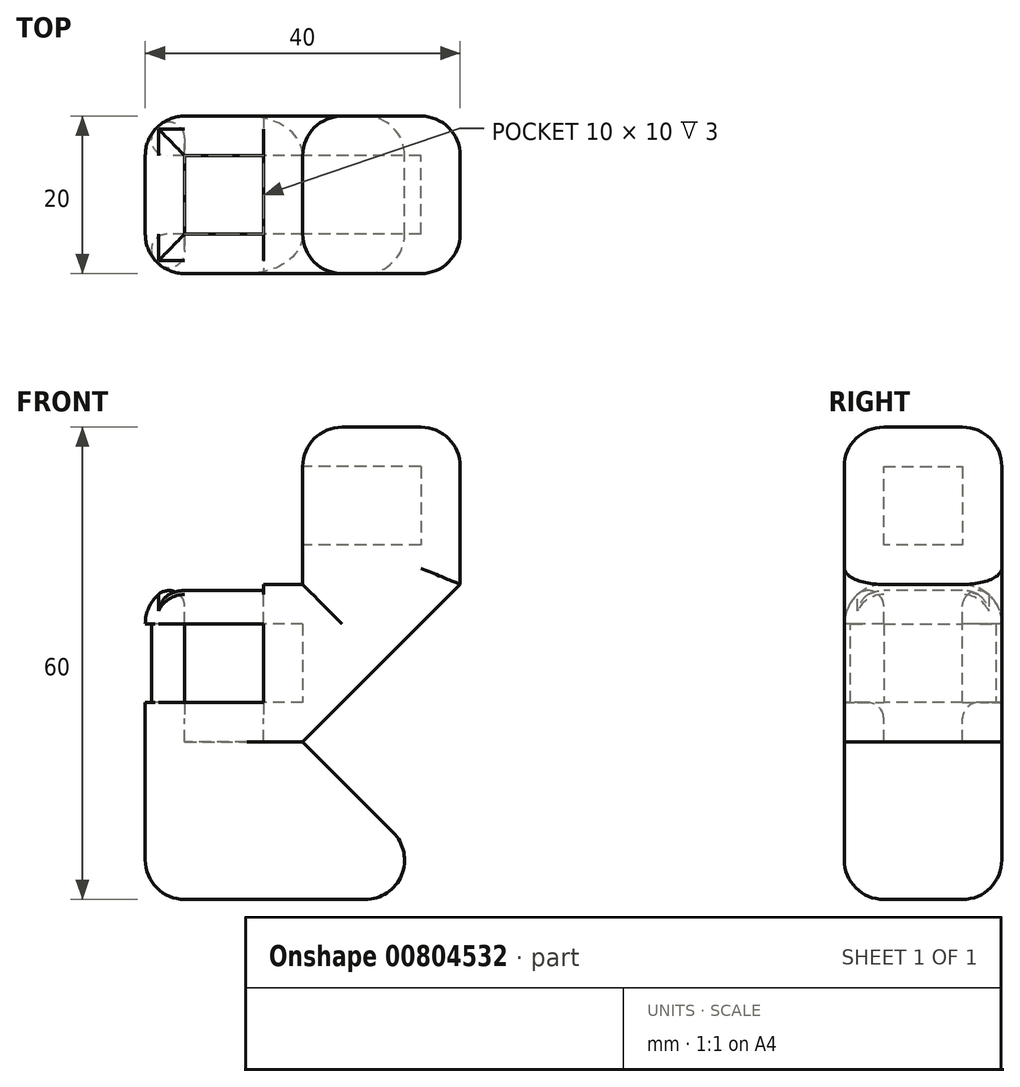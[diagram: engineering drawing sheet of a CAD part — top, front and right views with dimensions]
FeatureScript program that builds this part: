
annotation { "Feature Type Name" : "Feature", "Feature Type Description" : "" }
export const myFeature = defineFeature(function(context is Context, id is Id, definition is map)
    precondition{}
    {
        {
            var Q0;
            Q0=qCreatedBy(makeId("Front.planeOp"),FACE);
            var sketch = newSketch(context, id + "F0", { "sketchPlane" : qUnion([Q0])});
            skLineSegment(sketch, "E0.bottom", {"start": v(-64.5, 36.94) * mm, "end": v(-44.5, 36.94) * mm});
            skLineSegment(sketch, "E0.top", {"start": v(-64.5, 16.94) * mm, "end": v(-44.5, 16.94) * mm});
            skLineSegment(sketch, "E0.left", {"start": v(-64.5, 36.94) * mm, "end": v(-64.5, 16.94) * mm});
            skLineSegment(sketch, "E0.right", {"start": v(-44.5, 36.94) * mm, "end": v(-44.5, 16.94) * mm});
            skLineSegment(sketch, "E1.top", {"start": v(-64.5, 56.94) * mm, "end": v(-44.5, 56.94) * mm});
            skLineSegment(sketch, "E1.left", {"start": v(-64.5, 36.94) * mm, "end": v(-64.5, 56.94) * mm});
            skLineSegment(sketch, "E1.right", {"start": v(-44.5, 36.94) * mm, "end": v(-44.5, 56.94) * mm});
            skLineSegment(sketch, "E2", {"start": v(-44.5, 56.94) * mm, "end": v(-24.5, 56.94) * mm});
            skLineSegment(sketch, "E3", {"start": v(-24.5, 56.94) * mm, "end": v(-44.5, 36.94) * mm});
            skLineSegment(sketch, "E4.left", {"start": v(-44.5, 56.94) * mm, "end": v(-44.5, 56.94) * mm});
            skLineSegment(sketch, "E4.right", {"start": v(-24.5, 56.94) * mm, "end": v(-24.5, 56.94) * mm});
            skLineSegment(sketch, "E5.top", {"start": v(-44.5, 76.94) * mm, "end": v(-24.5, 76.94) * mm});
            skLineSegment(sketch, "E5.left", {"start": v(-44.5, 56.94) * mm, "end": v(-44.5, 76.94) * mm});
            skLineSegment(sketch, "E5.right", {"start": v(-24.5, 56.94) * mm, "end": v(-24.5, 76.94) * mm});
            skLineSegment(sketch, "E6", {"start": v(-44.5, 16.94) * mm, "end": v(-24.5, 16.94) * mm});
            skLineSegment(sketch, "E7", {"start": v(-24.5, 16.94) * mm, "end": v(-44.5, 36.94) * mm});
            skSolve(sketch);
        }
        {
            var Q0;
            Q0=makeQuery(id+"F0.imprint","IMPRINT",FACE,{"disambiguationData":[TD([[makeQuery(id+"F0.imprint","IMPRINT",EDGE,{"derivedFrom":sQuery(id+"F0.wireOp",EDGE,"E0.right")}),1.0]])]});
            var Q1;
            Q1=makeQuery(id+"F0.imprint","IMPRINT",FACE,{"disambiguationData":[TD([[makeQuery(id+"F0.imprint","IMPRINT",EDGE,{"derivedFrom":sQuery(id+"F0.wireOp",EDGE,"E0.top")}),1.0]])]});
            var Q2;
            Q2=makeQuery(id+"F0.imprint","IMPRINT",FACE,{"disambiguationData":[TD([[makeQuery(id+"F0.imprint","IMPRINT",EDGE,{"derivedFrom":sQuery(id+"F0.wireOp",EDGE,"E0.bottom")}),1.0]])]});
            var Q3;
            Q3=makeQuery(id+"F0.imprint","IMPRINT",FACE,{"disambiguationData":[TD([[makeQuery(id+"F0.imprint","IMPRINT",EDGE,{"derivedFrom":sQuery(id+"F0.wireOp",EDGE,"E1.right")}),-1.0]])]});
            var Q4;
            Q4=makeQuery(id+"F0.imprint","IMPRINT",FACE,{"disambiguationData":[TD([[makeQuery(id+"F0.imprint","IMPRINT",EDGE,{"derivedFrom":sQuery(id+"F0.wireOp",EDGE,"E2")}),1.0]])]});
            extrude(context, id + "F1", {"entities" : qUnion([Q0, Q1, Q2, Q3, Q4]), "depth" : 20 * mm, "offsetDistance" : 25 * mm});
        }
        {
            var Q0;
            Q0=makeQuery(id+"F1.opExtrude","SWEPT_FACE",FACE,{"disambiguationData":[OSD([sQuery(id+"F0.wireOp",EDGE,"E0.left"),sQuery(id+"F0.wireOp",EDGE,"E1.left")])]});
            var sketch = newSketch(context, id + "F2", { "sketchPlane" : qUnion([Q0])});
            skLineSegment(sketch, "E8", {"start": v(0, 56.94) * mm, "end": v(0, 36.94) * mm});
            skLineSegment(sketch, "E9", {"start": v(0, 36.94) * mm, "end": v(20, 36.94) * mm});
            skLineSegment(sketch, "E10", {"start": v(20, 36.94) * mm, "end": v(20, 56.94) * mm});
            skLineSegment(sketch, "E11", {"start": v(20, 56.94) * mm, "end": v(0, 56.94) * mm});
            skLineSegment(sketch, "E12.0", {"start": v(5, 51.94) * mm, "end": v(5, 41.94) * mm});
            skLineSegment(sketch, "E12.1", {"start": v(15, 51.94) * mm, "end": v(5, 51.94) * mm});
            skLineSegment(sketch, "E12.2", {"start": v(15, 41.94) * mm, "end": v(15, 51.94) * mm});
            skLineSegment(sketch, "E12.3", {"start": v(5, 41.94) * mm, "end": v(15, 41.94) * mm});
            skSolve(sketch);
        }
        {
            var Q0;
            Q0=makeQuery(id+"F2.imprint","IMPRINT",FACE,{"disambiguationData":[TD([[makeQuery(id+"F2.imprint","IMPRINT",EDGE,{"derivedFrom":sQuery(id+"F2.wireOp",EDGE,"E12.0")}),1.0]])]});
            extrude(context, id + "F3", {"entities" : qUnion([Q0]), "operationType" : NewBodyOperationType.REMOVE, "oppositeDirection" : true, "depth" : 20 * mm, "offsetDistance" : 25 * mm});
        }
        {
            var Q0;
            Q0=makeQuery(id+"F1.opExtrude","CAP_FACE",FACE,{"disambiguationData":[OSD([sQuery(id+"F0.wireOp",EDGE,"E0.top"),sQuery(id+"F0.wireOp",EDGE,"E0.left"),sQuery(id+"F0.wireOp",EDGE,"E1.top"),sQuery(id+"F0.wireOp",EDGE,"E1.left"),sQuery(id+"F0.wireOp",EDGE,"E3"),sQuery(id+"F0.wireOp",EDGE,"E5.top"),sQuery(id+"F0.wireOp",EDGE,"E5.left"),sQuery(id+"F0.wireOp",EDGE,"E5.right"),sQuery(id+"F0.wireOp",EDGE,"E6"),sQuery(id+"F0.wireOp",EDGE,"E7")])],"isStart":false});
            var sketch = newSketch(context, id + "F4", { "sketchPlane" : qUnion([Q0])});
            skLineSegment(sketch, "E13", {"start": v(-44.5, 36.94) * mm, "end": v(-64.5, 36.94) * mm});
            skLineSegment(sketch, "E14", {"start": v(-44.5, 36.94) * mm, "end": v(-44.5, 56.94) * mm});
            skLineSegment(sketch, "E15", {"start": v(-44.5, 56.94) * mm, "end": v(-64.5, 56.94) * mm});
            skLineSegment(sketch, "E16", {"start": v(-64.5, 56.94) * mm, "end": v(-64.5, 36.94) * mm});
            skLineSegment(sketch, "E17.0", {"start": v(-59.5, 51.94) * mm, "end": v(-59.5, 41.94) * mm});
            skLineSegment(sketch, "E17.1", {"start": v(-49.5, 51.94) * mm, "end": v(-59.5, 51.94) * mm});
            skLineSegment(sketch, "E17.2", {"start": v(-49.5, 41.94) * mm, "end": v(-49.5, 51.94) * mm});
            skLineSegment(sketch, "E17.3", {"start": v(-49.5, 41.94) * mm, "end": v(-59.5, 41.94) * mm});
            skSolve(sketch);
        }
        {
            var Q0;
            Q0=makeQuery(id+"F4.imprint","IMPRINT",FACE,{"disambiguationData":[TD([[makeQuery(id+"F4.imprint","IMPRINT",EDGE,{"derivedFrom":sQuery(id+"F4.wireOp",EDGE,"E17.0")}),1.0]])]});
            extrude(context, id + "F5", {"entities" : qUnion([Q0]), "operationType" : NewBodyOperationType.REMOVE, "oppositeDirection" : true, "depth" : 20 * mm, "offsetDistance" : 25 * mm});
        }
        {
            var Q0;
            Q0=makeQuery(id+"F1.opExtrude","SWEPT_FACE",FACE,{"disambiguationData":[OSD([sQuery(id+"F0.wireOp",EDGE,"E1.top")])]});
            var sketch = newSketch(context, id + "F6", { "sketchPlane" : qUnion([Q0])});
            skLineSegment(sketch, "E18.0", {"start": v(-49.5, -5) * mm, "end": v(-59.5, -5) * mm});
            skLineSegment(sketch, "E18.1", {"start": v(-49.5, -15) * mm, "end": v(-49.5, -5) * mm});
            skLineSegment(sketch, "E18.2", {"start": v(-59.5, -15) * mm, "end": v(-49.5, -15) * mm});
            skLineSegment(sketch, "E18.3", {"start": v(-59.5, -5) * mm, "end": v(-59.5, -15) * mm});
            skSolve(sketch);
        }
        {
            var Q0;
            Q0=makeQuery(id+"F6.imprint","IMPRINT",FACE,{"disambiguationData":[TD([[makeQuery(id+"F6.imprint","IMPRINT",EDGE,{"derivedFrom":sQuery(id+"F6.wireOp",EDGE,"E18.0")}),1.0]])]});
            extrude(context, id + "F7", {"entities" : qUnion([Q0]), "operationType" : NewBodyOperationType.REMOVE, "oppositeDirection" : true, "depth" : 20 * mm, "offsetDistance" : 25 * mm});
        }
        {
            var Q0;
            Q0=makeQuery(id+"F1.opExtrude","SWEPT_FACE",FACE,{"disambiguationData":[OSD([sQuery(id+"F0.wireOp",EDGE,"E5.left")])]});
            var sketch = newSketch(context, id + "F8", { "sketchPlane" : qUnion([Q0])});
            skLineSegment(sketch, "E19.0", {"start": v(5, 71.94) * mm, "end": v(5, 61.94) * mm});
            skLineSegment(sketch, "E19.1", {"start": v(15, 71.94) * mm, "end": v(5, 71.94) * mm});
            skLineSegment(sketch, "E19.2", {"start": v(15, 61.94) * mm, "end": v(15, 71.94) * mm});
            skLineSegment(sketch, "E19.3", {"start": v(5, 61.94) * mm, "end": v(15, 61.94) * mm});
            skSolve(sketch);
        }
        {
            var Q0;
            Q0=makeQuery(id+"F8.imprint","IMPRINT",FACE,{"disambiguationData":[TD([[makeQuery(id+"F8.imprint","IMPRINT",EDGE,{"derivedFrom":sQuery(id+"F8.wireOp",EDGE,"E19.0")}),1.0]])]});
            extrude(context, id + "F9", {"entities" : qUnion([Q0]), "operationType" : NewBodyOperationType.REMOVE, "oppositeDirection" : true, "depth" : 15 * mm, "offsetDistance" : 25 * mm});
        }
        {
            var Q0;
            Q0=makeQuery(id+"F1.opExtrude","CAP_EDGE",EDGE,{"disambiguationData":[OSD([sQuery(id+"F0.wireOp",EDGE,"E0.left"),sQuery(id+"F0.wireOp",EDGE,"E1.left")])],"isStart":false});
            var Q1;
            Q1=makeQuery(id+"F1.opExtrude","CAP_EDGE",EDGE,{"disambiguationData":[OSD([sQuery(id+"F0.wireOp",EDGE,"E0.left"),sQuery(id+"F0.wireOp",EDGE,"E1.left")])],"isStart":true});
            var Q2;
            Q2=makeQuery(id+"F1.opExtrude","SWEPT_EDGE",EDGE,{"disambiguationData":[OSD([sQuery(id+"F0.wireOp",EDGE,"E1.top"),sQuery(id+"F0.wireOp",EDGE,"E1.left")])]});
            var Q3;
            Q3=makeQuery(id+"F1.opExtrude","CAP_EDGE",EDGE,{"disambiguationData":[OSD([sQuery(id+"F0.wireOp",EDGE,"E1.top")])],"isStart":false});
            var Q4;
            Q4=makeQuery(id+"F1.opExtrude","CAP_EDGE",EDGE,{"disambiguationData":[OSD([sQuery(id+"F0.wireOp",EDGE,"E1.top")])],"isStart":true});
            var Q5;
            Q5=makeQuery(id+"F1.opExtrude","CAP_EDGE",EDGE,{"disambiguationData":[OSD([sQuery(id+"F0.wireOp",EDGE,"E7")])],"isStart":false});
            var Q6;
            Q6=makeQuery(id+"F1.opExtrude","CAP_EDGE",EDGE,{"disambiguationData":[OSD([sQuery(id+"F0.wireOp",EDGE,"E3")])],"isStart":false});
            var Q7;
            Q7=makeQuery(id+"F1.opExtrude","CAP_EDGE",EDGE,{"disambiguationData":[OSD([sQuery(id+"F0.wireOp",EDGE,"E7")])],"isStart":true});
            var Q8;
            Q8=makeQuery(id+"F1.opExtrude","CAP_EDGE",EDGE,{"disambiguationData":[OSD([sQuery(id+"F0.wireOp",EDGE,"E3")])],"isStart":true});
            var Q9;
            Q9=makeQuery(id+"F1.opExtrude","CAP_EDGE",EDGE,{"disambiguationData":[OSD([sQuery(id+"F0.wireOp",EDGE,"E5.right")])],"isStart":false});
            var Q10;
            Q10=makeQuery(id+"F1.opExtrude","CAP_EDGE",EDGE,{"disambiguationData":[OSD([sQuery(id+"F0.wireOp",EDGE,"E5.right")])],"isStart":true});
            var Q11;
            Q11=makeQuery(id+"F1.opExtrude","SWEPT_EDGE",EDGE,{"disambiguationData":[OSD([sQuery(id+"F0.wireOp",EDGE,"E5.top"),sQuery(id+"F0.wireOp",EDGE,"E5.left")])]});
            var Q12;
            Q12=makeQuery(id+"F1.opExtrude","CAP_EDGE",EDGE,{"disambiguationData":[OSD([sQuery(id+"F0.wireOp",EDGE,"E5.top")])],"isStart":false});
            var Q13;
            Q13=makeQuery(id+"F1.opExtrude","SWEPT_EDGE",EDGE,{"disambiguationData":[OSD([sQuery(id+"F0.wireOp",EDGE,"E5.top"),sQuery(id+"F0.wireOp",EDGE,"E5.right")])]});
            var Q14;
            Q14=makeQuery(id+"F1.opExtrude","CAP_EDGE",EDGE,{"disambiguationData":[OSD([sQuery(id+"F0.wireOp",EDGE,"E5.top")])],"isStart":true});
            var Q15;
            Q15=makeQuery(id+"F1.opExtrude","CAP_EDGE",EDGE,{"disambiguationData":[OSD([sQuery(id+"F0.wireOp",EDGE,"E0.top"),sQuery(id+"F0.wireOp",EDGE,"E6")])],"isStart":false});
            var Q16;
            Q16=makeQuery(id+"F1.opExtrude","CAP_EDGE",EDGE,{"disambiguationData":[OSD([sQuery(id+"F0.wireOp",EDGE,"E0.top"),sQuery(id+"F0.wireOp",EDGE,"E6")])],"isStart":true});
            var Q17;
            Q17=makeQuery(id+"F1.opExtrude","SWEPT_EDGE",EDGE,{"disambiguationData":[OSD([sQuery(id+"F0.wireOp",EDGE,"E6"),sQuery(id+"F0.wireOp",EDGE,"E7")])]});
            var Q18;
            Q18=makeQuery(id+"F1.opExtrude","SWEPT_EDGE",EDGE,{"disambiguationData":[OSD([sQuery(id+"F0.wireOp",EDGE,"E0.top"),sQuery(id+"F0.wireOp",EDGE,"E0.left")])]});
            fillet(context, id + "F10", {"entities" : qUnion([Q0, Q1, Q2, Q3, Q4, Q5, Q6, Q7, Q8, Q9, Q10, Q11, Q12, Q13, Q14, Q15, Q16, Q17, Q18]), "radius" : 5 * mm, "tangentPropagation" : true, "allowEdgeOverflow" : false});
        }
        {
            var Q0;
            Q0=makeQuery(id+"F5.boolean.opBoolean","COPY",EDGE,{"derivedFrom":makeQuery(id+"F5.opExtrude","CAP_EDGE",EDGE,{"disambiguationData":[OSD([sQuery(id+"F4.wireOp",EDGE,"E17.3")])],"isStart":true})});
            var Q1;
            Q1=makeQuery(id+"F3.boolean.opBoolean","COPY",EDGE,{"derivedFrom":makeQuery(id+"F3.opExtrude","CAP_EDGE",EDGE,{"disambiguationData":[OSD([sQuery(id+"F2.wireOp",EDGE,"E12.3")])],"isStart":true})});
            var Q2;
            Q2=makeQuery(id+"F5.boolean.opBoolean","COPY",EDGE,{"derivedFrom":makeQuery(id+"F5.opExtrude","CAP_EDGE",EDGE,{"disambiguationData":[OSD([sQuery(id+"F4.wireOp",EDGE,"E17.3")])],"isStart":false})});
            var Q3;
            Q3=makeQuery(id+"F7.boolean.opBoolean","INTERSECT",EDGE,{"derivedFrom":[makeQuery(id+"F5.boolean.opBoolean","MERGE",FACE,{"derivedFrom":[makeQuery(id+"F3.boolean.opBoolean","COPY",FACE,{"derivedFrom":makeQuery(id+"F3.opExtrude","SWEPT_FACE",FACE,{"disambiguationData":[OSD([sQuery(id+"F2.wireOp",EDGE,"E12.3")])]})}),makeQuery(id+"F5.opExtrude","SWEPT_FACE",FACE,{"disambiguationData":[OSD([sQuery(id+"F4.wireOp",EDGE,"E17.3")])]})]}),makeQuery(id+"F7.opExtrude","SWEPT_FACE",FACE,{"disambiguationData":[OSD([sQuery(id+"F6.wireOp",EDGE,"E18.2")])]})]});
            var Q4;
            Q4=makeQuery(id+"F7.boolean.opBoolean","INTERSECT",EDGE,{"derivedFrom":[makeQuery(id+"F5.boolean.opBoolean","MERGE",FACE,{"derivedFrom":[makeQuery(id+"F3.boolean.opBoolean","COPY",FACE,{"derivedFrom":makeQuery(id+"F3.opExtrude","SWEPT_FACE",FACE,{"disambiguationData":[OSD([sQuery(id+"F2.wireOp",EDGE,"E12.3")])]})}),makeQuery(id+"F5.opExtrude","SWEPT_FACE",FACE,{"disambiguationData":[OSD([sQuery(id+"F4.wireOp",EDGE,"E17.3")])]})]}),makeQuery(id+"F7.opExtrude","SWEPT_FACE",FACE,{"disambiguationData":[OSD([sQuery(id+"F6.wireOp",EDGE,"E18.0")])]})]});
            var Q5;
            {var subQ0=sQuery(id+"F0.wireOp",EDGE,"E1.left");var subQ1=sQuery(id+"F0.wireOp",EDGE,"E0.left");Q5=makeQuery(id+"F10.opFillet","BLEND_EDGE",EDGE,{"blendedFrom":[makeQuery(id+"F1.opExtrude","CAP_EDGE",EDGE,{"disambiguationData":[OSD([subQ1,subQ0])],"isStart":true}),makeQuery(id+"F5.boolean.opBoolean","SPLIT",FACE,{"disambiguationData":[TD([makeQuery(id+"F5.opExtrude","SWEPT_FACE",FACE,{"disambiguationData":[OSD([sQuery(id+"F4.wireOp",EDGE,"E17.0")])]})])],"derivedFrom":makeQuery(id+"F3.boolean.opBoolean","COPY",FACE,{"derivedFrom":makeQuery(id+"F3.opExtrude","SWEPT_FACE",FACE,{"disambiguationData":[OSD([sQuery(id+"F2.wireOp",EDGE,"E12.0")])]})})})],"blendedInto":[makeQuery(id+"F5.boolean.opBoolean","SPLIT",FACE,{"disambiguationData":[TD([makeQuery(id+"F5.opExtrude","SWEPT_FACE",FACE,{"disambiguationData":[OSD([sQuery(id+"F4.wireOp",EDGE,"E17.0")])]})])],"derivedFrom":makeQuery(id+"F3.boolean.opBoolean","COPY",FACE,{"derivedFrom":makeQuery(id+"F3.opExtrude","SWEPT_FACE",FACE,{"disambiguationData":[OSD([sQuery(id+"F2.wireOp",EDGE,"E12.0")])]})})})]});}
            var Q6;
            {var subQ0=sQuery(id+"F0.wireOp",EDGE,"E1.left");var subQ1=sQuery(id+"F0.wireOp",EDGE,"E0.left");Q6=makeQuery(id+"F10.opFillet","BLEND_EDGE",EDGE,{"blendedFrom":[makeQuery(id+"F1.opExtrude","CAP_EDGE",EDGE,{"disambiguationData":[OSD([subQ1,subQ0])],"isStart":false}),makeQuery(id+"F5.boolean.opBoolean","SPLIT",FACE,{"disambiguationData":[TD([makeQuery(id+"F5.opExtrude","SWEPT_FACE",FACE,{"disambiguationData":[OSD([sQuery(id+"F4.wireOp",EDGE,"E17.0")])]})])],"derivedFrom":makeQuery(id+"F3.boolean.opBoolean","COPY",FACE,{"derivedFrom":makeQuery(id+"F3.opExtrude","SWEPT_FACE",FACE,{"disambiguationData":[OSD([sQuery(id+"F2.wireOp",EDGE,"E12.2")])]})})})],"blendedInto":[makeQuery(id+"F5.boolean.opBoolean","SPLIT",FACE,{"disambiguationData":[TD([makeQuery(id+"F5.opExtrude","SWEPT_FACE",FACE,{"disambiguationData":[OSD([sQuery(id+"F4.wireOp",EDGE,"E17.0")])]})])],"derivedFrom":makeQuery(id+"F3.boolean.opBoolean","COPY",FACE,{"derivedFrom":makeQuery(id+"F3.opExtrude","SWEPT_FACE",FACE,{"disambiguationData":[OSD([sQuery(id+"F2.wireOp",EDGE,"E12.2")])]})})})]});}
            var Q7;
            {var subQ0=sQuery(id+"F0.wireOp",EDGE,"E1.left");var subQ1=sQuery(id+"F0.wireOp",EDGE,"E0.left");Q7=makeQuery(id+"F10.opFillet","BLEND_EDGE",EDGE,{"blendedFrom":[makeQuery(id+"F1.opExtrude","CAP_EDGE",EDGE,{"disambiguationData":[OSD([subQ1,subQ0])],"isStart":true}),makeQuery(id+"F5.boolean.opBoolean","COPY",FACE,{"disambiguationData":[TD([makeQuery(id+"F3.boolean.opBoolean","COPY",FACE,{"derivedFrom":makeQuery(id+"F3.opExtrude","SWEPT_FACE",FACE,{"disambiguationData":[OSD([sQuery(id+"F2.wireOp",EDGE,"E12.0")])]})})])],"derivedFrom":makeQuery(id+"F5.opExtrude","SWEPT_FACE",FACE,{"disambiguationData":[OSD([sQuery(id+"F4.wireOp",EDGE,"E17.0")])]})})],"blendedInto":[makeQuery(id+"F5.boolean.opBoolean","COPY",FACE,{"disambiguationData":[TD([makeQuery(id+"F3.boolean.opBoolean","COPY",FACE,{"derivedFrom":makeQuery(id+"F3.opExtrude","SWEPT_FACE",FACE,{"disambiguationData":[OSD([sQuery(id+"F2.wireOp",EDGE,"E12.0")])]})})])],"derivedFrom":makeQuery(id+"F5.opExtrude","SWEPT_FACE",FACE,{"disambiguationData":[OSD([sQuery(id+"F4.wireOp",EDGE,"E17.0")])]})})]});}
            fillet(context, id + "F11", {"entities" : qUnion([Q0, Q1, Q2, Q3, Q4, Q5, Q6, Q7]), "radius" : 2 * mm, "tangentPropagation" : true, "allowEdgeOverflow" : false});
        }
        {
            var Q0;
            Q0=makeQuery(id+"F1.opExtrude","CAP_EDGE",EDGE,{"disambiguationData":[OSD([sQuery(id+"F0.wireOp",EDGE,"E5.left")])],"isStart":true});
            var Q1;
            Q1=makeQuery(id+"F1.opExtrude","CAP_EDGE",EDGE,{"disambiguationData":[OSD([sQuery(id+"F0.wireOp",EDGE,"E5.left")])],"isStart":false});
            fillet(context, id + "F12", {"entities" : qUnion([Q0, Q1]), "radius" : 5 * mm, "tangentPropagation" : true, "allowEdgeOverflow" : false});
        }
    });
